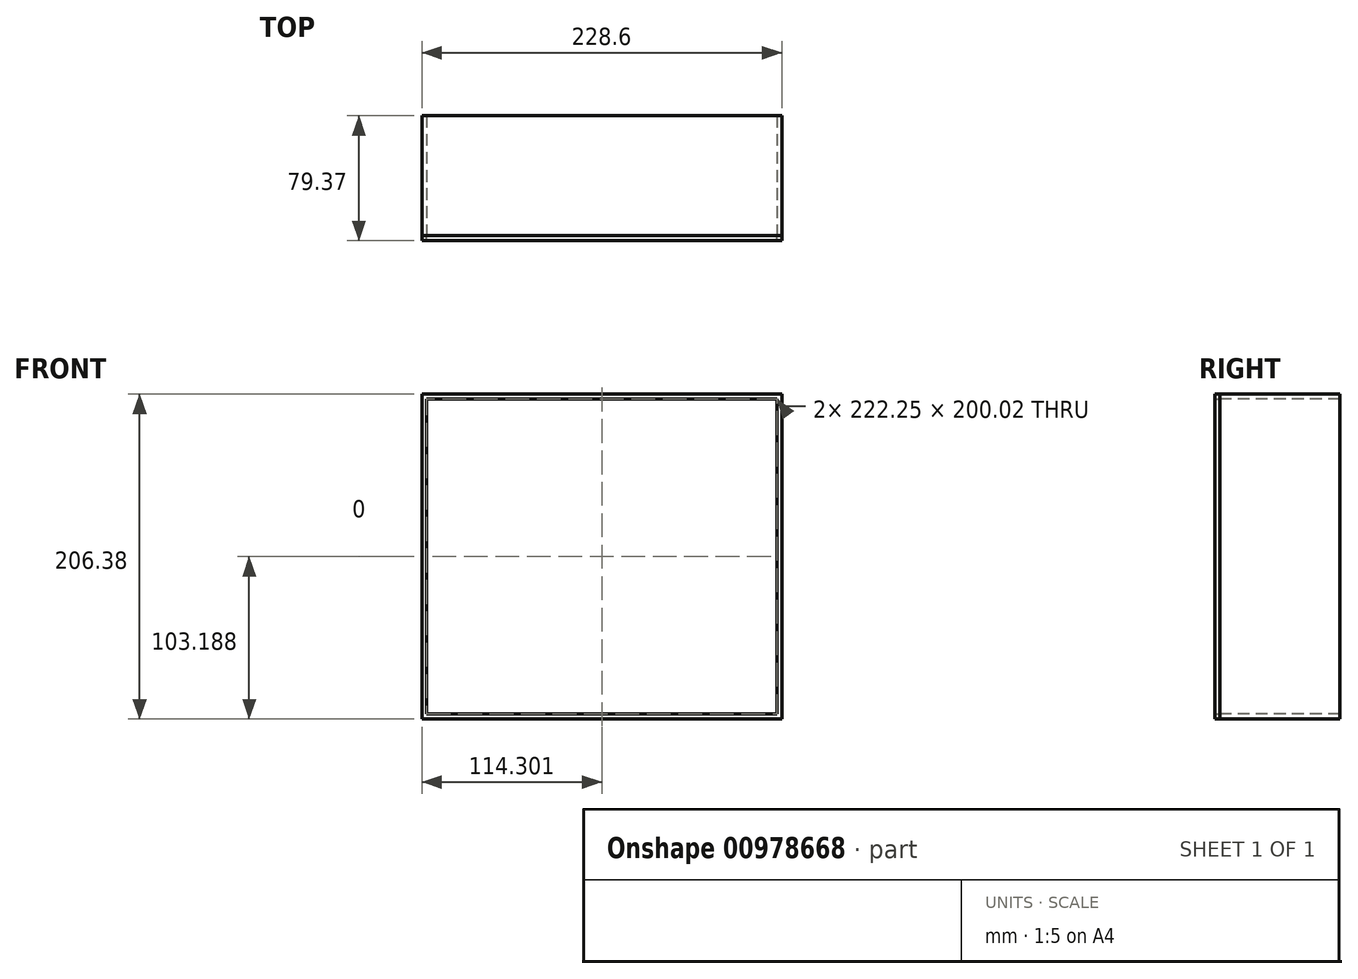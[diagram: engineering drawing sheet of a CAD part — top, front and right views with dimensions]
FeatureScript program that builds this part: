
annotation { "Feature Type Name" : "Feature", "Feature Type Description" : "" }
export const myFeature = defineFeature(function(context is Context, id is Id, definition is map)
    precondition{}
    {
        {
            var Q0;
            Q0=qCreatedBy(makeId("Top.planeOp"),FACE);
            var sketch = newSketch(context, id + "F0", { "sketchPlane" : qUnion([Q0])});
            skLineSegment(sketch, "E0.bottom", {"start": v(-102.24, 19.74) * mm, "end": v(126.36, 19.74) * mm});
            skLineSegment(sketch, "E0.top", {"start": v(-102.24, -56.46) * mm, "end": v(126.36, -56.46) * mm});
            skLineSegment(sketch, "E0.left", {"start": v(-102.24, 19.74) * mm, "end": v(-102.24, -56.46) * mm});
            skLineSegment(sketch, "E0.right", {"start": v(126.36, 19.74) * mm, "end": v(126.36, -56.46) * mm});
            skSolve(sketch);
        }
        {
            var Q0;
            Q0 = qSketchRegion(id + "F0", true);
            extrude(context, id + "F1", {"entities" : qUnion([Q0]), "depth" : 3.17 * mm, "offsetDistance" : 25.4 * mm});
        }
        {
            var Q0;
            Q0=makeQuery(id+"F1.opExtrude","SWEPT_FACE",FACE,{"disambiguationData":[OSD([sQuery(id+"F0.wireOp",EDGE,"E0.left")])]});
            var sketch = newSketch(context, id + "F2", { "sketchPlane" : qUnion([Q0])});
            skLineSegment(sketch, "E1.bottom", {"start": v(56.46, 3.17) * mm, "end": v(-19.74, 3.17) * mm});
            skLineSegment(sketch, "E1.top", {"start": v(56.46, 206.38) * mm, "end": v(-19.74, 206.38) * mm});
            skLineSegment(sketch, "E1.left", {"start": v(56.46, 3.18) * mm, "end": v(56.46, 206.38) * mm});
            skLineSegment(sketch, "E1.right", {"start": v(-19.74, 3.17) * mm, "end": v(-19.74, 206.38) * mm});
            skSolve(sketch);
        }
        {
            var Q0;
            Q0 = qSketchRegion(id + "F2", true);
            extrude(context, id + "F3", {"entities" : qUnion([Q0]), "oppositeDirection" : true, "depth" : 3.17 * mm, "offsetDistance" : 25.4 * mm});
        }
        {
            var Q0;
            Q0=makeQuery(id+"F1.opExtrude","SWEPT_FACE",FACE,{"disambiguationData":[OSD([sQuery(id+"F0.wireOp",EDGE,"E0.right")])]});
            cPlane(context, id + "F4", {"entities" : qUnion([Q0]), "cplaneType" : CPlaneType.OFFSET, "offset" : 114.3 * mm, "oppositeDirection" : true, "width" : 152.4 * mm, "height" : 152.4 * mm});
        }
        {
            var Q0;
            Q0=makeQuery(id+"F3.opExtrude","SWEPT_BODY",BODY,{"disambiguationData":[OSD([sQuery(id+"F2.wireOp",EDGE,"E1.bottom"),sQuery(id+"F2.wireOp",EDGE,"E1.top"),sQuery(id+"F2.wireOp",EDGE,"E1.left"),sQuery(id+"F2.wireOp",EDGE,"E1.right")])]});
            var Q1;
            Q1=qCreatedBy(id+"F4.planeOp",FACE);
            mirror(context, id + "F5", {"operationType" : NewBodyOperationType.ADD, "entities" : qUnion([Q0]), "mirrorPlane" : qUnion([Q1])});
        }
        {
            var Q0;
            Q0=makeQuery(id+"F5.opPattern","COPY",FACE,{"derivedFrom":makeQuery(id+"F3.opExtrude","SWEPT_FACE",FACE,{"disambiguationData":[OSD([sQuery(id+"F2.wireOp",EDGE,"E1.top")])]}),"instanceName":"1"});
            var Q1;
            Q1=makeQuery(id+"F1.opExtrude","CAP_FACE",FACE,{"disambiguationData":[OSD([sQuery(id+"F0.wireOp",EDGE,"E0.bottom"),sQuery(id+"F0.wireOp",EDGE,"E0.top"),sQuery(id+"F0.wireOp",EDGE,"E0.left"),sQuery(id+"F0.wireOp",EDGE,"E0.right")])],"isStart":true});
            cPlane(context, id + "F6", {"entities" : qUnion([Q0, Q1]), "cplaneType" : CPlaneType.MID_PLANE, "offset" : 25.4 * mm, "width" : 152.4 * mm, "height" : 152.4 * mm});
        }
        {
            var Q0;
            Q0=makeQuery(id+"F1.opExtrude","SWEPT_BODY",BODY,{"disambiguationData":[OSD([sQuery(id+"F0.wireOp",EDGE,"E0.bottom"),sQuery(id+"F0.wireOp",EDGE,"E0.top"),sQuery(id+"F0.wireOp",EDGE,"E0.left"),sQuery(id+"F0.wireOp",EDGE,"E0.right")])]});
            var Q1;
            Q1=qCreatedBy(id+"F6.planeOp",FACE);
            mirror(context, id + "F7", {"operationType" : NewBodyOperationType.ADD, "entities" : qUnion([Q0]), "mirrorPlane" : qUnion([Q1])});
        }
        {
            var Q0;
            {var subQ0=makeQuery(id+"F3.opExtrude","SWEPT_FACE",FACE,{"disambiguationData":[OSD([sQuery(id+"F2.wireOp",EDGE,"E1.left")])]});var subQ1=makeQuery(id+"F5.boolean.opBoolean","MERGE",FACE,{"derivedFrom":[makeQuery(id+"F1.opExtrude","SWEPT_FACE",FACE,{"disambiguationData":[OSD([sQuery(id+"F0.wireOp",EDGE,"E0.top")])]}),subQ0,makeQuery(id+"F5.opPattern","COPY",FACE,{"derivedFrom":subQ0,"instanceName":"1"})]});Q0=makeQuery(id+"F7.boolean.opBoolean","MERGE",FACE,{"derivedFrom":[subQ1,makeQuery(id+"F7.opPattern","COPY",FACE,{"derivedFrom":subQ1,"instanceName":"1"})]});}
            var sketch = newSketch(context, id + "F8", { "sketchPlane" : qUnion([Q0])});
            skLineSegment(sketch, "E2.bottom", {"start": v(-99.06, 203.2) * mm, "end": v(123.19, 203.2) * mm});
            skLineSegment(sketch, "E2.top", {"start": v(-99.06, 3.18) * mm, "end": v(123.19, 3.18) * mm});
            skLineSegment(sketch, "E2.left", {"start": v(-99.06, 203.2) * mm, "end": v(-99.06, 3.17) * mm});
            skLineSegment(sketch, "E2.right", {"start": v(123.19, 203.2) * mm, "end": v(123.19, 3.17) * mm});
            skSolve(sketch);
        }
        {
            var Q0;
            Q0 = qSketchRegion(id + "F8", true);
            extrude(context, id + "F9", {"entities" : qUnion([Q0]), "depth" : 3.17 * mm, "offsetDistance" : 25.4 * mm});
        }
        {
            var Q0;
            {var subQ0=makeQuery(id+"F3.opExtrude","SWEPT_FACE",FACE,{"disambiguationData":[OSD([sQuery(id+"F2.wireOp",EDGE,"E1.left")])]});var subQ1=makeQuery(id+"F5.boolean.opBoolean","MERGE",FACE,{"derivedFrom":[makeQuery(id+"F1.opExtrude","SWEPT_FACE",FACE,{"disambiguationData":[OSD([sQuery(id+"F0.wireOp",EDGE,"E0.top")])]}),subQ0,makeQuery(id+"F5.opPattern","COPY",FACE,{"derivedFrom":subQ0,"instanceName":"1"})]});Q0=makeQuery(id+"F7.boolean.opBoolean","MERGE",FACE,{"derivedFrom":[subQ1,makeQuery(id+"F7.opPattern","COPY",FACE,{"derivedFrom":subQ1,"instanceName":"1"})]});}
            var sketch = newSketch(context, id + "F10", { "sketchPlane" : qUnion([Q0])});
            skLineSegment(sketch, "E3.bottom", {"start": v(126.36, 0) * mm, "end": v(-102.24, 0) * mm});
            skLineSegment(sketch, "E3.top", {"start": v(126.36, 206.38) * mm, "end": v(-102.24, 206.38) * mm});
            skLineSegment(sketch, "E3.left", {"start": v(126.36, 0) * mm, "end": v(126.36, 206.38) * mm});
            skLineSegment(sketch, "E3.right", {"start": v(-102.24, 0) * mm, "end": v(-102.24, 206.38) * mm});
            skLineSegment(sketch, "E4.bottom", {"start": v(123.19, 3.18) * mm, "end": v(-99.06, 3.18) * mm});
            skLineSegment(sketch, "E4.top", {"start": v(123.19, 203.2) * mm, "end": v(-99.06, 203.2) * mm});
            skLineSegment(sketch, "E4.left", {"start": v(123.19, 3.17) * mm, "end": v(123.19, 203.2) * mm});
            skLineSegment(sketch, "E4.right", {"start": v(-99.06, 3.17) * mm, "end": v(-99.06, 203.2) * mm});
            skSolve(sketch);
        }
        {
            var Q0;
            Q0 = qSketchRegion(id + "F10", true);
            var Q1;
            Q1=makeQuery(id+"F9.opExtrude","CAP_FACE",FACE,{"disambiguationData":[OSD([sQuery(id+"F8.wireOp",EDGE,"E2.bottom"),sQuery(id+"F8.wireOp",EDGE,"E2.top"),sQuery(id+"F8.wireOp",EDGE,"E2.left"),sQuery(id+"F8.wireOp",EDGE,"E2.right")])],"isStart":false});
            extrude(context, id + "F11", {"entities" : qUnion([Q0]), "endBound" : BoundingType.UP_TO_SURFACE, "depth" : 25.4 * mm, "endBoundEntityFace" : qUnion([Q1]), "offsetDistance" : 25.4 * mm});
        }
    });
